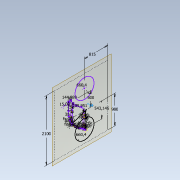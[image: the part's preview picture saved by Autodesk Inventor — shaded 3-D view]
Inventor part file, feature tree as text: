
AUTODESK INVENTOR PART (.ipt)
format: ipt  version: 2021 (Build 250183000, 183)  size: 1,078,272 bytes
history: native  units: mm
features: sketch x3, other x2, plane x1
ambient origin geometry x8: Origin, YZ Plane, XZ Plane, XY Plane, X Axis, Y Axis, Z Axis, Center Point
feature tree (6):
  sketch  "Boceto 3D1"  dims[d3=509.95112mm]
  sketch  "Boceto 3D2"  dims[d100=144.888874mm]
  sketch  "Boceto 3D3"  dims[d154=500.0mm d175=47.5mm d176=47.5mm d177=47.5mm d178=47.5mm d179=47.5mm d180=30.0mm d208=6.0mm d210=47.5mm d211=35.0mm d212=65.0mm d213=47.5mm d214=47.5mm d216=660.4mm d217=660.4mm d234=980.0mm d236=2100.0mm d237=815.0mm d277=70.0mm]
  plane  "Plano de trabajo1"
  other  "Punto de trabajo1"
  other  "Imagen2"
